# Revit family: SAE301
name_source: partatom
category: Lighting Fixtures
revit_build: Autodesk Revit 2014 (Build: 20130308_1515(x64)
units: mm (PartAtom-declared; Revit-internal decimal feet)

## types (3) — shared parameters
Apparent Load = 17 VA
Assembly Code = D5020200
Backbox = Hubbell- Paint - Matte White
Ceiling Type = 15/16” Grid Ceiling; 9/16” Narrow Face Grid Ceiling; 9/16” Screw Slot Grid Ceiling; Drywall Ceiling
Color Filter = 16777215
Default Elevation = 48 "
Description = SAE301 is a versatile, recessed, direct enclosed troffer, available in 3 sizes
Diffuser = Soft Glow Lens
Dimming Lamp Color Temperature Shift = <None>
Distribution = Direct
Emit Shape Visible in Rendering = No
Glass = Hubbell - White Glass
Lamp = LED
Load Classification = Lighting
Manufacturer = Litecontrol Lighting
Model = SAE301
Mounting = Recessed
Nominal Watts = 17 W
Photometric Link = https://www.hubbell.com
Photometric Notes = More IES files download on Photometric Link
Photometric Web File = SAE301-X-D-14-SGL-CX-35K-D19.ies
Power Factor = 1
Product Documentation Link = https://hubbellcdn.com
Product Page URL = https://www.hubbell.com
Tilt Angle = -90.00°
Type Comments = Lighting Fixture
URL = https://www.hubbell.com
Voltage = 120 V
Warranty = 5 years warranty
Wattage Comments = 133 Lumens/Watt

## per-type parameters (varying)
| type | Emit from Rectangle Length | Emit from Rectangle Width | zz Length 1 | zz Length 2 |
| SAE301-1x4 | 47 " | 4 " | 48 " | 12 " |
| SAE301-2x2 | 23 " | 16 " | 24 " | 24 " |
| SAE301-2x4 | 47 " | 16 " | 48 " | 24 " |

## geometry (parser evidence)
native form markers: Sweep x2
no freeform markers — native parametric forms only
